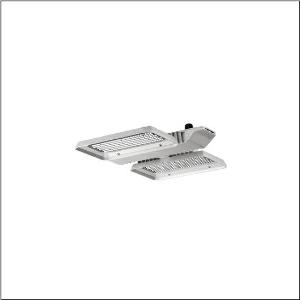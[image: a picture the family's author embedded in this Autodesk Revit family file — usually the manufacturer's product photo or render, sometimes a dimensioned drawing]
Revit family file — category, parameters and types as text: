
# Revit family: highbay_11_51hla1d14fca
name_source: partatom
category: Lighting Fixtures
units: mm (PartAtom-declared; Revit-internal decimal feet)

## family parameters
Cut with Voids When Loaded = No
Host = Face
Light Source = No
Part Type = Normal
Room Calculation Point = No
Round Connector Dimension = Use Diameter
Shared = No

## types (1)
- --- (1 x LED, 14060 lm, 81.2 W, 4000K)
    Apparent Load = 81 VA
    CIE Flux Codes = 88 95 99 100 99
    Color Rendering = 80
    Color Temperature = 4000K
    Default Elevation = 1800 mm
    Description = Highbay 11, LED high bay luminaire, primary light control with lens, of PMMA, light emission: direct distribution, primary light characteristic: symmetric, installation type: surface-mounted, suspended mounting, for 1x 2x LED, rated luminous flux: 14.060lm, luminous efficacy: 173lm/W, light colour: 840, colour temperature: 4000K, control gear: ECG DALI, with terminal, 5-pole, max. 2.5mm², mains connection: 230..240V, AC, 50/60Hz, rated input power: 81W, LED unit, of diecast aluminium, unplated, bead blasted, silver, length: 470mm, width: 500mm, height: 65mm, housing, of diecast aluminium, uncoated, bead blasted, silver, protection rating (complete): IP65, insulation class (complete): insulation class I (protective earthing), certification: CE, ENEC, VDE, UKCA, protection symbol: D, impact resistance: IK08 with glass or PC cover, permissible operating ambient temperature: -35..+55°C, reducing of maximum allowable ambient temperature of 5°C with ceiling mounting, corresponds to IFS (International Featured Standards) requirements for safety and quality in the food industry, packaging unit: 1 piece
    Height = 95 mm
    Lamp = 1 x LED
    Lamp Light Flux = 14060 lm
    Lamp Power = 81.2 W
    Lamp count = 1
    Length = 468 mm
    Luminous efficacy = 173 lm/W
    Manufacturer = Siteco
    ModVariant = No
    Model = 51HLA1D14FCA
    Mounting Place = Ceiling
    Mounting Type = Pendant
    Number of Poles = 1
    OnlyDefault = Yes
    Power Factor = 1
    Product Name = Highbay 11
    Product group = LED high bay luminaire
    ProductGroupID = 903
    Protection Class = Protection class I
    Protection Degree = IP 65
    RLX_Detail_Level = 1
    RLX_Emergency_Light_Flux = 0 lm
    RLX_Emergency_Type = 0
    RLX_Emergency_Type_DB = No
    RlxData = <blob elided: 89957 chars, md5=fb132291>
    Socket = socket
    Standby Power = 0 W
    System Light Flux = 14060 lm
    System Power = 81 W
    Type Comments = factory setting: luminous flux: 100 % | dim-lin: 254 | 460 mA
    Type Image = l_1003425.jpg
    URL = http://relux.com
    VarID = @adj_160331
    Voltage = 0 V
    Weight = 0.00 kg
    Width = 501 mm

## geometry (parser evidence)
native form markers: Blend x4, Sweep x14
no freeform markers — native parametric forms only
